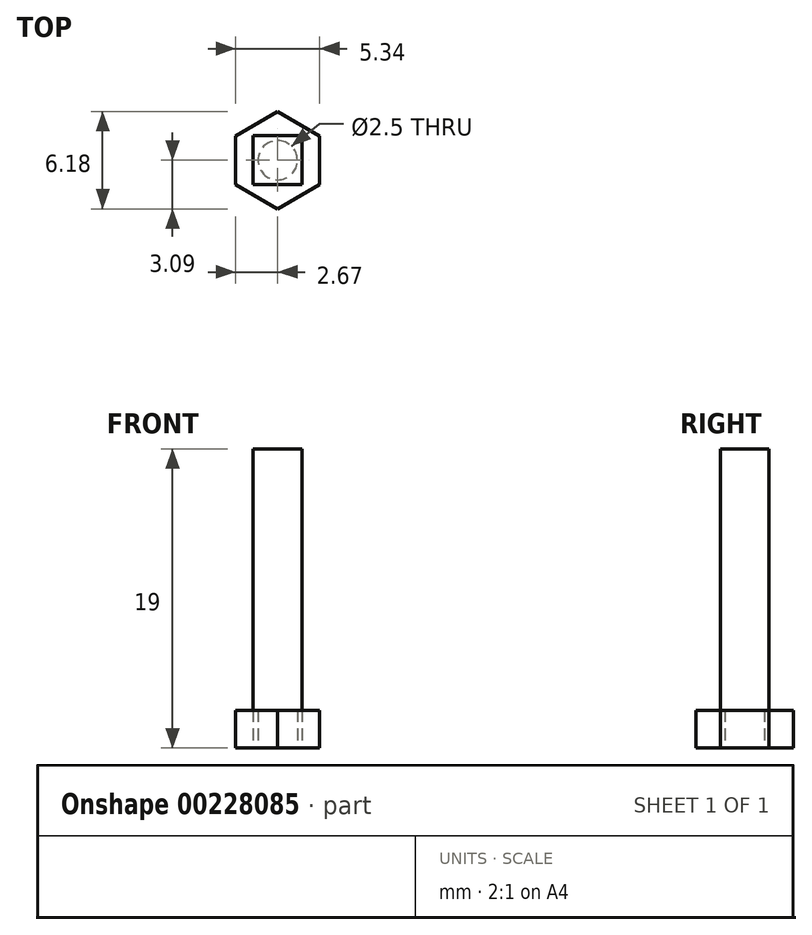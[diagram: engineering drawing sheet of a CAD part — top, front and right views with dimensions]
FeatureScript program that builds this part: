
annotation { "Feature Type Name" : "Feature", "Feature Type Description" : "" }
export const myFeature = defineFeature(function(context is Context, id is Id, definition is map)
    precondition{}
    {
        {
            var Q0;
            Q0=qCreatedBy(makeId("Top.planeOp"),FACE);
            var sketch = newSketch(context, id + "F0", { "sketchPlane" : qUnion([Q0])});
            skLineSegment(sketch, "E0.bottom", {"start": v(1.55, -1.55) * mm, "end": v(-1.55, -1.55) * mm});
            skLineSegment(sketch, "E0.top", {"start": v(1.55, 1.55) * mm, "end": v(-1.55, 1.55) * mm});
            skLineSegment(sketch, "E0.left", {"start": v(1.55, -1.55) * mm, "end": v(1.55, 1.55) * mm});
            skLineSegment(sketch, "E0.right", {"start": v(-1.55, -1.55) * mm, "end": v(-1.55, 1.55) * mm});
            skPoint(sketch, "E0.middle", {"position": v(0, 0) * mm});
            skSolve(sketch);
        }
        {
            var Q0;
            Q0 = qSketchRegion(id + "F0", true);
            extrude(context, id + "F1", {"entities" : qUnion([Q0]), "depth" : 19 * mm});
        }
        {
            var Q0;
            Q0=qCreatedBy(makeId("Top.planeOp"),FACE);
            var sketch = newSketch(context, id + "F2", { "sketchPlane" : qUnion([Q0])});
            skCircle(sketch, "E1.cCircle", {"center": v(0, 0) * mm, "radius": 3.09 * mm, "construction": true});
            skLineSegment(sketch, "E1.0", {"start": v(2.68, -1.54) * mm, "end": v(0, -3.09) * mm});
            skLineSegment(sketch, "E1.1", {"start": v(0, -3.09) * mm, "end": v(-2.68, -1.54) * mm});
            skLineSegment(sketch, "E1.2", {"start": v(-2.68, -1.54) * mm, "end": v(-2.67, 1.54) * mm});
            skLineSegment(sketch, "E1.3", {"start": v(-2.68, 1.54) * mm, "end": v(0, 3.09) * mm});
            skLineSegment(sketch, "E1.4", {"start": v(0, 3.09) * mm, "end": v(2.68, 1.54) * mm});
            skLineSegment(sketch, "E1.5", {"start": v(2.68, 1.54) * mm, "end": v(2.67, -1.54) * mm});
            skCircle(sketch, "E2", {"center": v(0, 0) * mm, "radius": 1.25 * mm});
            skSolve(sketch);
        }
        {
            var Q0;
            Q0 = qSketchRegion(id + "F2", true);
            extrude(context, id + "F3", {"entities" : qUnion([Q0]), "depth" : 2.4 * mm});
        }
    });
